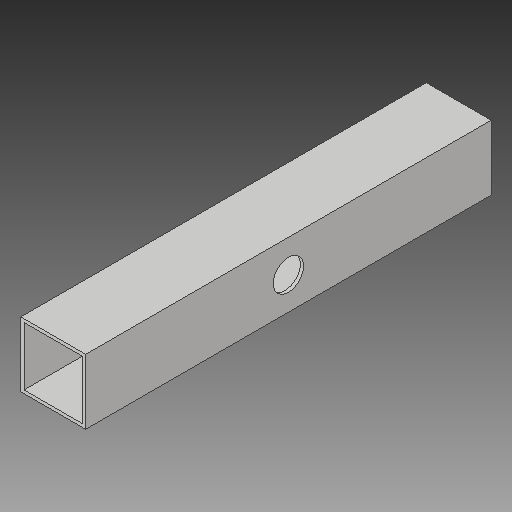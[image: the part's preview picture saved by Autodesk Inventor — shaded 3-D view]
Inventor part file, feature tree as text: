
AUTODESK INVENTOR PART (.ipt)
format: ipt  version: 2018 (Build 220112000, 112)  size: 106,496 bytes
history: native  units: mm
features: other x2, sketch x2, extrude x1, hole x1
ambient origin geometry x8: Origin, YZ Plane, XZ Plane, XY Plane, X Axis, Y Axis, Z Axis, Center Point
bodies: Body1 (feature_tree)
feature tree (6):
  other  "ソリッド1"
  extrude  "押し出し1"  Depth=32.0mm
  other  "作業平面1"
  hole  "穴1"  [1 undecoded]
  sketch  "スケッチ1"
  sketch  "スケッチ2"
note: 1 required parameter value undecoded (feature->parameter linkage not recoverable at this tier; creation-order binding heuristic only, values carry confidence <= 0.55)
